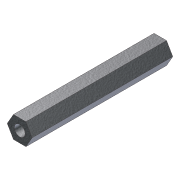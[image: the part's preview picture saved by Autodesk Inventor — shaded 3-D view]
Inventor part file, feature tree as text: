
AUTODESK INVENTOR PART (.ipt)
format: ipt  version: 2012 (Build 160160000, 160)  size: 90,624 bytes
history: native  units: in
note: dims shown in document units (in); Inventor stores cm internally (conversion verified against a paired STEP export)
features: extrude x3, sketch x3
ambient origin geometry x8: Origin, YZ Plane, XZ Plane, XY Plane, X Axis, Y Axis, Z Axis, Center Point
bodies: Solid1 (feature_tree)
feature tree (6):
  extrude  "Extrusion1"  Depth=3.25in TaperAngle=0.0deg
  extrude  "Extrusion2"  Depth=1.0in TaperAngle=0.0deg
  extrude  "Extrusion3"  Depth=1.0in TaperAngle=0.0deg
  sketch  "Sketch1"  dims[d0=0.5in d1=3.25in d2=0.0in]
  sketch  "Sketch3"  dims[d4=0.25in d5=1.0in d6=0.0in]
  sketch  "Sketch4"  dims[d7=0.25in d8=1.0in d9=0.0in]
